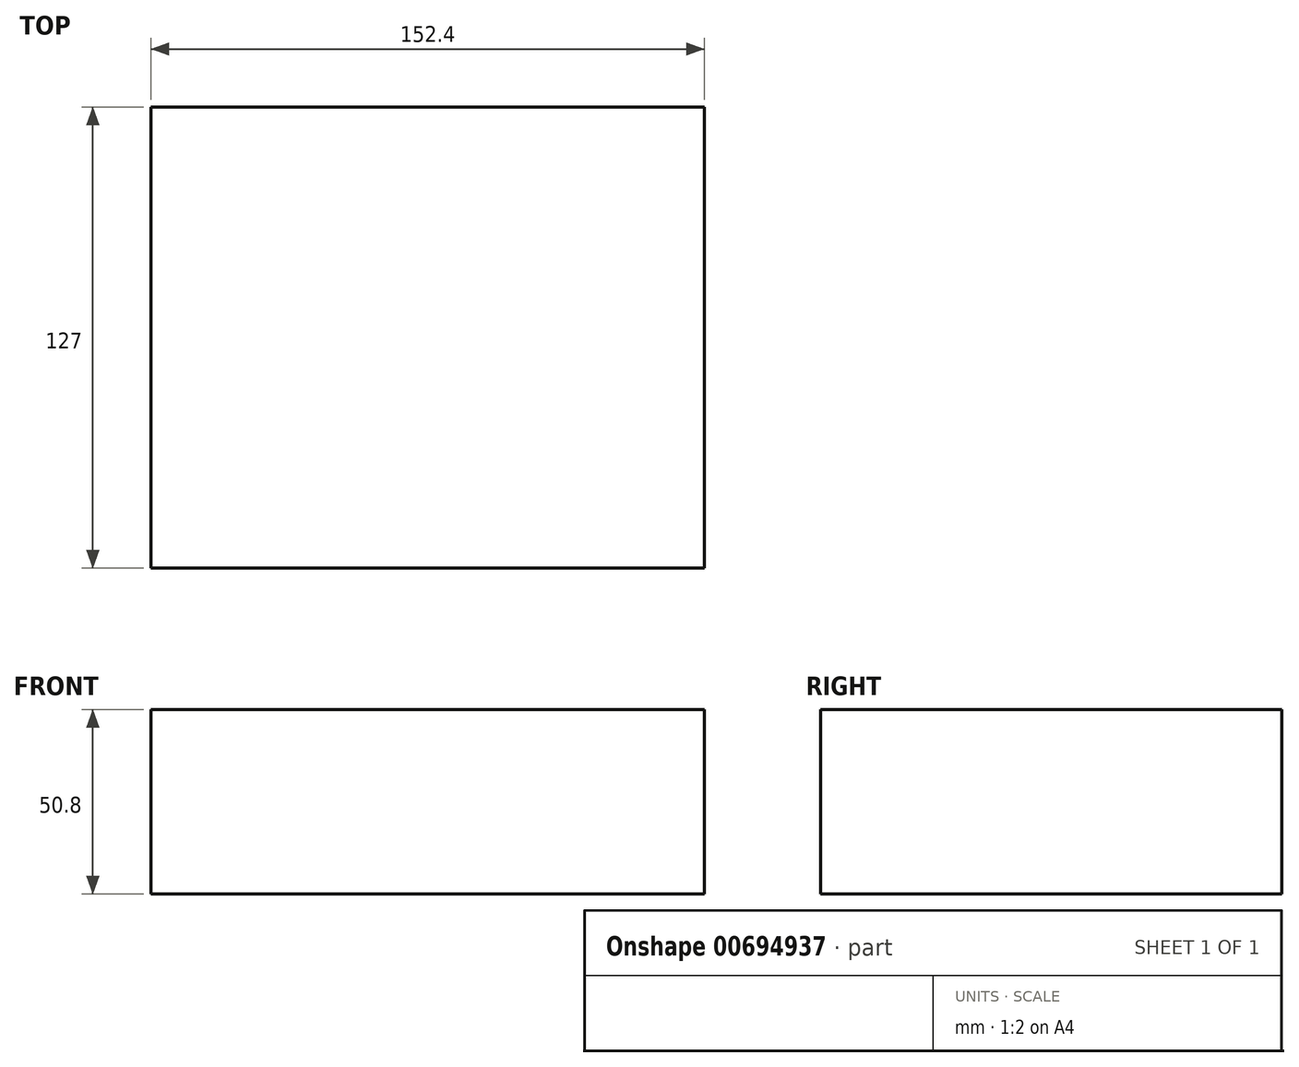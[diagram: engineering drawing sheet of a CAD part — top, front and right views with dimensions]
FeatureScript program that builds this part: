
annotation { "Feature Type Name" : "Feature", "Feature Type Description" : "" }
export const myFeature = defineFeature(function(context is Context, id is Id, definition is map)
    precondition{}
    {
        {
            var Q0;
            Q0=qCreatedBy(makeId("Front.planeOp"),FACE);
            var sketch = newSketch(context, id + "F0", { "sketchPlane" : qUnion([Q0])});
            skLineSegment(sketch, "E0.bottom", {"start": v(-50.8, -38.1) * mm, "end": v(101.6, -38.1) * mm});
            skLineSegment(sketch, "E0.top", {"start": v(-50.8, 12.7) * mm, "end": v(101.6, 12.7) * mm});
            skLineSegment(sketch, "E0.left", {"start": v(-50.8, -38.1) * mm, "end": v(-50.8, 12.7) * mm});
            skLineSegment(sketch, "E0.right", {"start": v(101.6, -38.1) * mm, "end": v(101.6, 12.7) * mm});
            skLineSegment(sketch, "E1.bottom", {"start": v(-50.8, 12.7) * mm, "end": v(0, 12.7) * mm});
            skLineSegment(sketch, "E1.top", {"start": v(-50.8, 63.5) * mm, "end": v(0, 63.5) * mm});
            skLineSegment(sketch, "E1.left", {"start": v(-50.8, 12.7) * mm, "end": v(-50.8, 63.5) * mm});
            skLineSegment(sketch, "E1.right", {"start": v(0, 12.7) * mm, "end": v(0, 63.5) * mm});
            skLineSegment(sketch, "E2.bottom", {"start": v(101.6, 12.7) * mm, "end": v(50.8, 12.7) * mm});
            skLineSegment(sketch, "E2.top", {"start": v(101.6, 63.5) * mm, "end": v(50.8, 63.5) * mm});
            skLineSegment(sketch, "E2.left", {"start": v(101.6, 12.7) * mm, "end": v(101.6, 63.5) * mm});
            skLineSegment(sketch, "E2.right", {"start": v(50.8, 12.7) * mm, "end": v(50.8, 63.5) * mm});
            skSolve(sketch);
        }
        {
            var Q0;
            Q0=makeQuery(id+"F0.imprint","IMPRINT",FACE,{"disambiguationData":[TD([[makeQuery(id+"F0.imprint","IMPRINT",EDGE,{"derivedFrom":sQuery(id+"F0.wireOp",EDGE,"E1.bottom")}),1.0]])]});
            var Q1;
            Q1=makeQuery(id+"F0.imprint","IMPRINT",FACE,{"disambiguationData":[TD([[makeQuery(id+"F0.imprint","IMPRINT",EDGE,{"derivedFrom":sQuery(id+"F0.wireOp",EDGE,"E0.bottom")}),1.0]])]});
            var Q2;
            Q2=makeQuery(id+"F0.imprint","IMPRINT",FACE,{"disambiguationData":[TD([[makeQuery(id+"F0.imprint","IMPRINT",EDGE,{"derivedFrom":sQuery(id+"F0.wireOp",EDGE,"E2.bottom")}),-1.0]])]});
            extrude(context, id + "F1", {"entities" : qUnion([Q0, Q1, Q2]), "depth" : 127 * mm, "offsetDistance" : 25.4 * mm});
        }
    });
